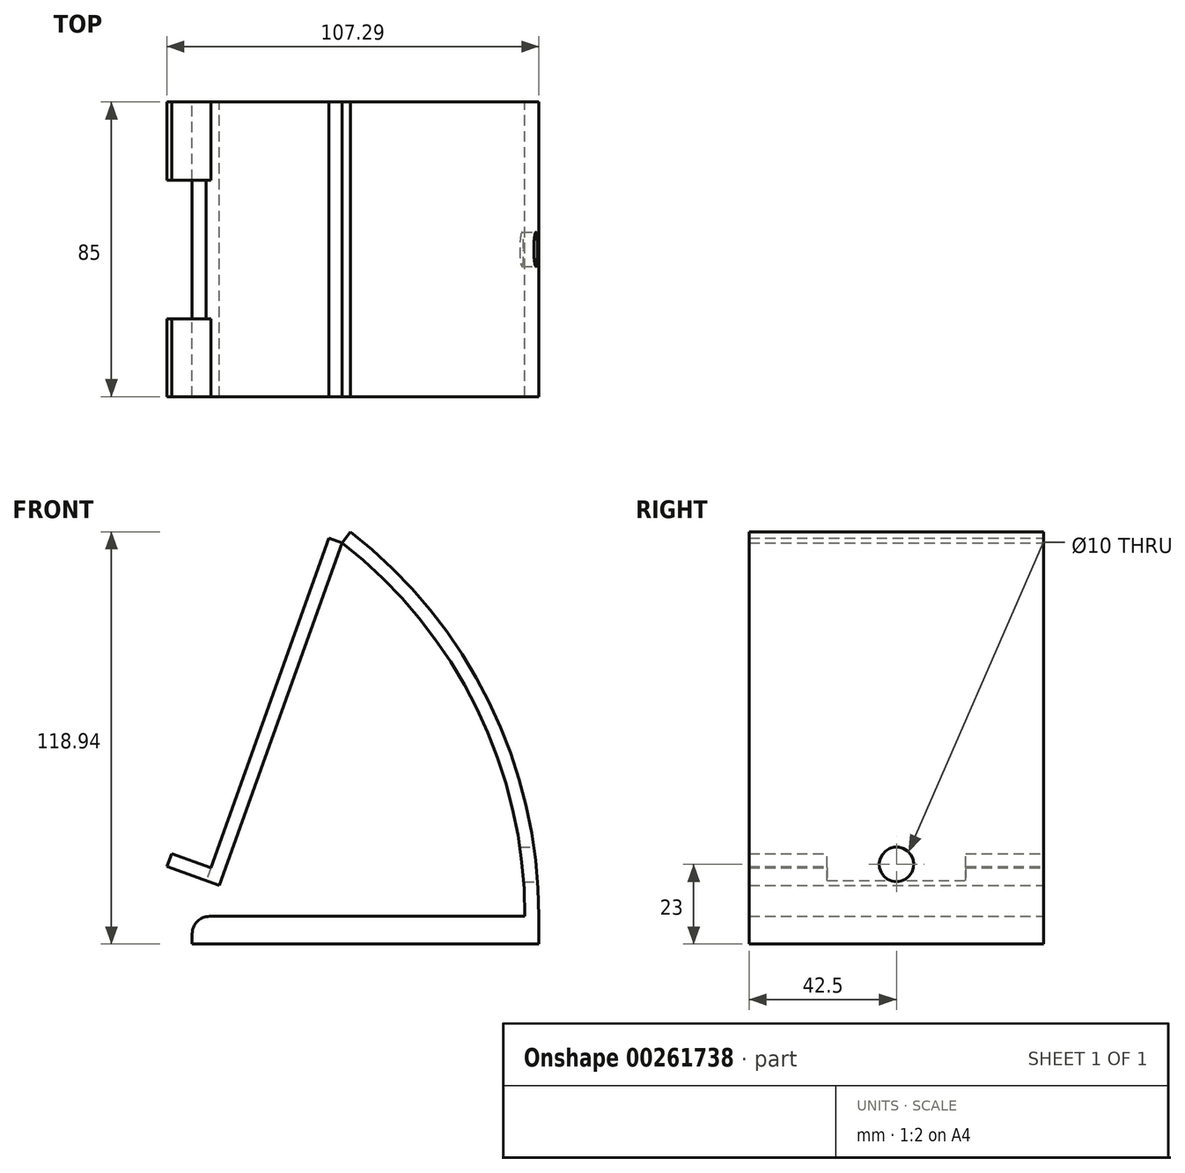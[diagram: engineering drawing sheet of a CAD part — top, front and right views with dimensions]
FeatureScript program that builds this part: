
annotation { "Feature Type Name" : "Feature", "Feature Type Description" : "" }
export const myFeature = defineFeature(function(context is Context, id is Id, definition is map)
    precondition{}
    {
        {
            var Q0;
            Q0=qCreatedBy(makeId("Front.planeOp"),FACE);
            var sketch = newSketch(context, id + "F0", { "sketchPlane" : qUnion([Q0])});
            skLineSegment(sketch, "E0.bottom", {"start": v(50, -4) * mm, "end": v(-50, -4) * mm});
            skLineSegment(sketch, "E0.top", {"start": v(50, 4) * mm, "end": v(-45, 4) * mm});
            skLineSegment(sketch, "E0.left", {"start": v(50, -4) * mm, "end": v(50, 4) * mm});
            skLineSegment(sketch, "E0.right", {"start": v(-50, -4) * mm, "end": v(-50, -1) * mm});
            skPoint(sketch, "E0.middle", {"position": v(0, 0) * mm});
            skArc(sketch, "E1", {"start": v(50, 4) * mm, "mid": v(35.7, 65.76) * mm, "end": v(-4.31, 114.94) * mm});
            skArc(sketch, "E2.0", {"start": v(46, 4) * mm, "mid": v(32.1, 64) * mm, "end": v(-6.76, 111.78) * mm});
            skLineSegment(sketch, "E3", {"start": v(-6.76, 111.78) * mm, "end": v(-42.23, 12.95) * mm});
            skLineSegment(sketch, "E4.0", {"start": v(-10.53, 113.13) * mm, "end": v(-46, 14.3) * mm});
            skArc(sketch, "E5", {"start": v(-10.53, 113.13) * mm, "mid": v(-7.88, 115.62) * mm, "end": v(-4.31, 114.94) * mm});
            skLineSegment(sketch, "E6", {"start": v(-6.76, 111.78) * mm, "end": v(-10.53, 113.13) * mm});
            skLineSegment(sketch, "E7", {"start": v(-6.76, 111.78) * mm, "end": v(-4.31, 114.94) * mm});
            skLineSegment(sketch, "E8", {"start": v(-46, 14.3) * mm, "end": v(-42.23, 12.95) * mm});
            skLineSegment(sketch, "E9", {"start": v(-46, 14.3) * mm, "end": v(-57.3, 18.36) * mm});
            skLineSegment(sketch, "E10.0", {"start": v(-44.65, 18.07) * mm, "end": v(-55.94, 22.12) * mm});
            skLineSegment(sketch, "E11", {"start": v(-57.3, 18.36) * mm, "end": v(-55.94, 22.12) * mm});
            skPoint(sketch, "E12.visualSharp", {"position": v(-50, 4) * mm});
            skArc(sketch, "E12.filletArc", {"start": v(-45, 4) * mm, "mid": v(-48.54, 2.54) * mm, "end": v(-50, -1) * mm});
            skSolve(sketch);
        }
        {
            var Q0;
            {var subQ0=sQuery(id+"F0.wireOp",EDGE,"dAroDJ6w-FwDb-7C3O-hDjj-gmL6Na2V3lde");Q0=makeQuery(id+"F0.imprint","IMPRINT",FACE,{"disambiguationData":[TD([[makeQuery(id+"F0.imprint","IMPRINT",EDGE,{"derivedFrom":subQ0}),-1.0]])]});}
            var Q1;
            Q1=makeQuery(id+"F0.imprint","IMPRINT",FACE,{"disambiguationData":[TD([[makeQuery(id+"F0.imprint","IMPRINT",EDGE,{"derivedFrom":sQuery(id+"F0.wireOp",EDGE,"E0.bottom")}),-1.0]])]});
            var Q2;
            Q2=makeQuery(id+"F0.imprint","IMPRINT",FACE,{"disambiguationData":[TD([[makeQuery(id+"F0.imprint","IMPRINT",EDGE,{"derivedFrom":sQuery(id+"F0.wireOp",EDGE,"E5")}),-1.0]])]});
            var Q3;
            {var subQ0=sQuery(id+"F0.wireOp",EDGE,"E1");Q3=makeQuery(id+"F0.imprint","IMPRINT",FACE,{"disambiguationData":[TD([[makeQuery(id+"F0.imprint","IMPRINT",EDGE,{"derivedFrom":subQ0}),1.0]])]});}
            var Q4;
            Q4=makeQuery(id+"F0.imprint","IMPRINT",FACE,{"disambiguationData":[TD([[makeQuery(id+"F0.imprint","IMPRINT",EDGE,{"derivedFrom":sQuery(id+"F0.wireOp",EDGE,"E3")}),-1.0]])]});
            var Q5;
            {var subQ0=sQuery(id+"F0.wireOp",EDGE,"E9");Q5=makeQuery(id+"F0.imprint","IMPRINT",FACE,{"disambiguationData":[TD([[makeQuery(id+"F0.imprint","IMPRINT",EDGE,{"derivedFrom":subQ0}),-1.0]])]});}
            extrude(context, id + "F1", {"entities" : qUnion([Q0, Q1, Q2, Q3, Q4, Q5]), "depth" : 85 * mm});
        }
        {
            var Q0;
            {var subQ0=sQuery(id+"F0.wireOp",EDGE,"E9");Q0=makeQuery(id+"F0.imprint","IMPRINT",FACE,{"disambiguationData":[TD([[makeQuery(id+"F0.imprint","IMPRINT",EDGE,{"derivedFrom":subQ0}),-1.0]])]});}
            extrude(context, id + "F2", {"entities" : qUnion([Q0]), "operationType" : NewBodyOperationType.REMOVE, "depth" : 62.5 * mm, "hasSecondDirection" : true, "secondDirectionOppositeDirection" : false, "secondDirectionDepth" : 22.5 * mm});
        }
        {
            var Q0;
            Q0=makeQuery(id+"F1.opExtrude","SWEPT_FACE",FACE,{"disambiguationData":[OSD([sQuery(id+"F0.wireOp",EDGE,"E0.left")])]});
            var sketch = newSketch(context, id + "F3", { "sketchPlane" : qUnion([Q0])});
            skLineSegment(sketch, "E13", {"start": v(-42.5, 4) * mm, "end": v(-42.5, 19) * mm, "construction": true});
            skPoint(sketch, "E13.endSnap0", {"position": v(-42.5, 4) * mm});
            skSolve(sketch);
        }
        {
            var Q0;
            Q0=sQuery(id+"F3.wireOp",VERTEX,"E13.end");
            var Q1;
            Q1=makeQuery(id+"F1.opExtrude","SWEPT_BODY",BODY,{"disambiguationData":[OSD([sQuery(id+"F0.wireOp",EDGE,"E0.bottom"),sQuery(id+"F0.wireOp",EDGE,"E0.top"),sQuery(id+"F0.wireOp",EDGE,"E0.left"),sQuery(id+"F0.wireOp",EDGE,"E0.right"),sQuery(id+"F0.wireOp",EDGE,"E1"),sQuery(id+"F0.wireOp",EDGE,"E2.0"),sQuery(id+"F0.wireOp",EDGE,"E3"),sQuery(id+"F0.wireOp",EDGE,"E4.0"),sQuery(id+"F0.wireOp",EDGE,"E5"),sQuery(id+"F0.wireOp",EDGE,"E8"),sQuery(id+"F0.wireOp",EDGE,"E9"),sQuery(id+"F0.wireOp",EDGE,"E10.0"),sQuery(id+"F0.wireOp",EDGE,"E11"),sQuery(id+"F0.wireOp",EDGE,"E12.filletArc")])]});
            hole(context, id + "F4", {"style" : HoleStyle.SIMPLE, "endStyle" : HoleEndStyle.BLIND, "holeDiameter" : 10 * mm, "holeDepth" : 12 * mm, "tappedDepth" : 12 * mm, "tapClearance" : 3, "locations" : qUnion([Q0]), "scope" : qUnion([Q1])});
        }
    });
